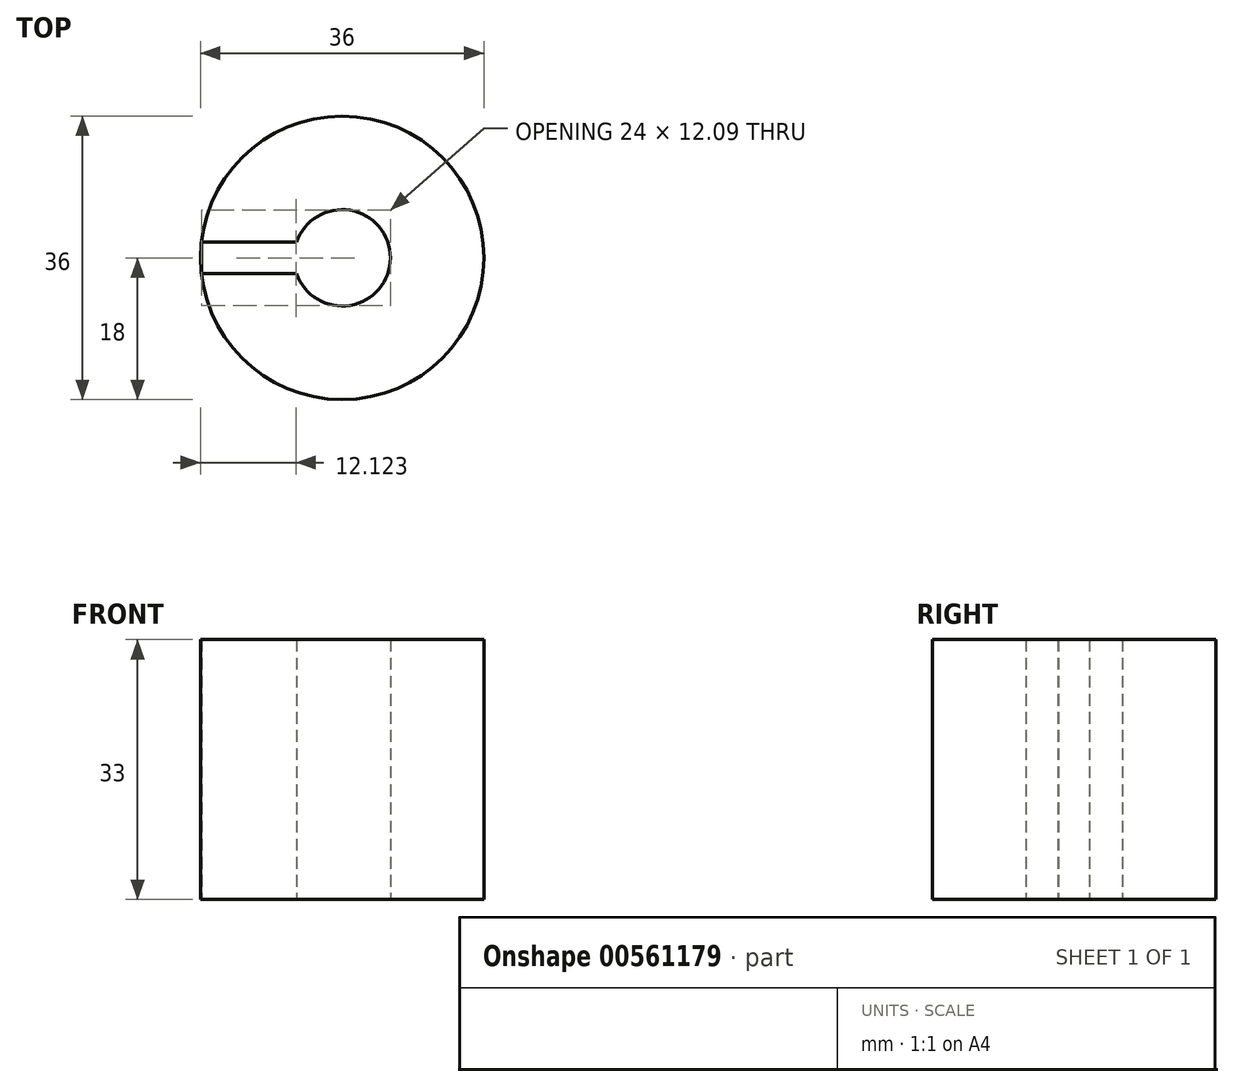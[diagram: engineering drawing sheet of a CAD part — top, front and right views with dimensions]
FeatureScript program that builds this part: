
annotation { "Feature Type Name" : "Feature", "Feature Type Description" : "" }
export const myFeature = defineFeature(function(context is Context, id is Id, definition is map)
    precondition{}
    {
        {
            var Q0;
            Q0=qCreatedBy(makeId("Top.planeOp"),FACE);
            var sketch = newSketch(context, id + "F0", { "sketchPlane" : qUnion([Q0])});
            skCircle(sketch, "E0", {"center": v(0, 0) * mm, "radius": 18 * mm});
            skCircle(sketch, "E1", {"center": v(0, 0) * mm, "radius": 6.12 * mm});
            skLineSegment(sketch, "E2.bottom", {"start": v(-5.8, 1.98) * mm, "end": v(-17.88, 1.98) * mm});
            skLineSegment(sketch, "E2.top", {"start": v(-5.8, -2.02) * mm, "end": v(-17.88, -2.02) * mm});
            skLineSegment(sketch, "E2.left", {"start": v(-5.8, 1.98) * mm, "end": v(-5.8, -2.02) * mm});
            skLineSegment(sketch, "E2.right", {"start": v(-17.88, 1.98) * mm, "end": v(-17.88, -2.02) * mm});
            skSolve(sketch);
        }
        {
            var Q0;
            {var subQ0=sQuery(id+"F0.wireOp",EDGE,"E2.right");var subQ1=sQuery(id+"F0.wireOp",EDGE,"E0");var subQ2=makeQuery(id+"F0.imprint","INTERSECT",VERTEX,{"disambiguationData":[OD(0.0)],"derivedFrom":[subQ1,subQ0]});Q0=makeQuery(id+"F0.imprint","IMPRINT",FACE,{"disambiguationData":[TD([[makeQuery(id+"F0.imprint","IMPRINT",EDGE,{"disambiguationData":[TD([[subQ2,1.0]])],"derivedFrom":subQ1}),-1.0]])]});}
            var Q1;
            {var subQ0=sQuery(id+"F0.wireOp",EDGE,"E2.right");var subQ1=sQuery(id+"F0.wireOp",EDGE,"E0");var subQ2=makeQuery(id+"F0.imprint","INTERSECT",VERTEX,{"disambiguationData":[OD(1.0)],"derivedFrom":[subQ1,subQ0]});Q1=makeQuery(id+"F0.imprint","IMPRINT",FACE,{"disambiguationData":[TD([[makeQuery(id+"F0.imprint","IMPRINT",EDGE,{"disambiguationData":[TD([[subQ2,-1.0]])],"derivedFrom":subQ1}),-1.0]])]});}
            var Q2;
            {var subQ1=sQuery(id+"F0.wireOp",EDGE,"E2.bottom");var subQ4=sQuery(id+"F0.wireOp",EDGE,"E0");var subQ5=makeQuery(id+"F0.imprint","INTERSECT",VERTEX,{"derivedFrom":[subQ4,subQ1]});Q2=makeQuery(id+"F0.imprint","IMPRINT",FACE,{"disambiguationData":[TD([[makeQuery(id+"F0.imprint","IMPRINT",EDGE,{"disambiguationData":[TD([[subQ5,1.0]])],"derivedFrom":subQ4}),1.0]])]});}
            extrude(context, id + "F1", {"entities" : qUnion([Q0, Q1, Q2]), "depth" : 33 * mm, "offsetDistance" : 25 * mm});
        }
    });
